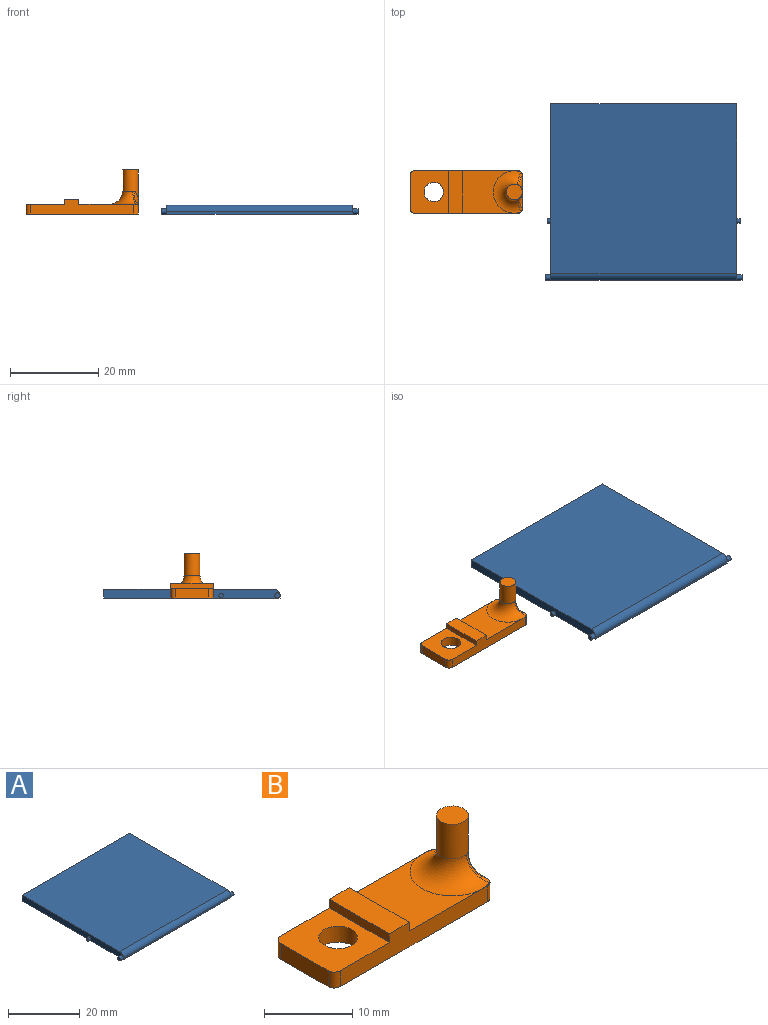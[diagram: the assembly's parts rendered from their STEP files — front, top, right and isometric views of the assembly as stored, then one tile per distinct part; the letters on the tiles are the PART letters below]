
ASSEMBLY  parts=2 mates=1
PART A: 17 faces, bbox 44.6x40x2 mm
  f0: plane 39.98x2mm, normal (1,0,0), area 77.5mm2, adj f3,f6,f7,f12,f14,f16
  f1: plane 39.98x2mm, normal (-1,0,0), area 77.5mm2, adj f3,f6,f7,f8,f10,f16
  f2: plane 0.6x0.56mm, normal (1,0,0), area 0.1mm2, adj f5,f7,f12,f16
  f3: plane 42.2x2mm, normal (0,1,0), area 84.4mm2, adj f0,f1,f6,f7
  f4: plane 0.6x0.56mm, normal (-1,0,0), area 0.1mm2, adj f5,f7,f8,f16
  f5: plane 42.2x0.5mm, normal (0,-1,0), area 21.1mm2, adj f2,f4,f7,f16
  f6: plane 42.2x38.5mm, normal (0,0,1), area 1624.7mm2, adj f0,f1,f3,f16
  f7: plane 42.2x40mm, normal (0,0,-1), area 1688mm2, adj f0,f1,f2,f3,f4,f5
  f8: cylinder r=0.6mm len=1.2mm, axis (1,0,0), area 4.5mm2, adj f1,f4,f9,f16
  f9: plane 1.2x1.2mm, normal (-1,0,0), area 1.1mm2, adj f8
  f10: cylinder r=0.5mm len=1mm, axis (1,0,0), area 2.5mm2, adj f1,f11
  f11: plane 1x1mm, normal (-1,0,0), area 0.8mm2, adj f10
  f12: cylinder r=0.6mm len=1.2mm, axis (-1,0,0), area 4.5mm2, adj f0,f2,f13,f16
  f13: plane 1.2x1.2mm, normal (1,0,0), area 1.1mm2, adj f12
  f14: cylinder r=0.5mm len=1mm, axis (-1,0,0), area 2.5mm2, adj f0,f15
  f15: plane 1x1mm, normal (1,0,0), area 0.8mm2, adj f14
  f16: cylinder r=1.5mm len=42.2mm, axis (-1,0,0), area 99.4mm2, adj f0,f1,f2,f4,f5,f6,f8,f12
PART B: 24 faces, bbox 25.9x15x10 mm
  f0: plane 11.7x9.6mm, normal (0,0,1), area 76.1mm2, adj f5,f9,f17,f22
  f1: plane 1.42x0.21mm, normal (0,0,1), area 0.1mm2, adj f9,f10,f17
  f2: plane 9.6x8.8mm, normal (0,0,1), area 68.8mm2, adj f5,f6,f7,f8,f9,f20,f21
  f3: plane 7.6x2.2mm, normal (1,0,0), area 16.7mm2, adj f4,f10,f12,f15,f19
  f4: cylinder r=1mm len=2.2mm, axis (0,0,-1), area 3.5mm2, adj f3,f5,f11,f12,f18
  f5: plane 23.5x3.4mm, normal (0,1,0), area 55.5mm2, adj f0,f2,f4,f6,f11,f12,f21,f22
  f6: cylinder r=1mm len=2.2mm, axis (0,0,-1), area 3.5mm2, adj f2,f5,f7,f12
  f7: plane 7.6x2.2mm, normal (-1,0,0), area 16.7mm2, adj f2,f6,f8,f12
  f8: cylinder r=1mm len=2.2mm, axis (0,0,-1), area 3.5mm2, adj f2,f7,f9,f12
  f9: plane 23.5x3.4mm, normal (0,-1,0), area 55.5mm2, adj f0,f1,f2,f8,f10,f12,f21,f22
  f10: cylinder r=1mm len=2.2mm, axis (0,0,-1), area 3.5mm2, adj f1,f3,f9,f12,f16
  f11: plane 1.42x0.21mm, normal (0,0,1), area 0.1mm2, adj f4,f5,f17
  f12: plane 25.5x9.6mm, normal (0,0,-1), area 228.7mm2, adj f3,f4,f5,f6,f7,f8,f9,f10
  f13: cylinder r=1.8mm len=7.8mm, axis (0,0,-1), area 59.7mm2, adj f14,f15,f16,f17,f18,f19
  f14: plane 3.6x3.6mm, normal (0,0,1), area 10.2mm2, adj f13
  f15: bspline ~3.92x2.84mm, area 4.9mm2, adj f3,f13,f16
  f16: bspline ~3.34x3.06mm, area 2mm2, adj f10,f13,f15,f17
  f17: torus R=4.8mm, axis (0,0,1), area 51mm2, adj f0,f1,f11,f13,f16,f18
  f18: bspline ~3.33x3.05mm, area 2mm2, adj f4,f13,f17,f19
  f19: bspline ~3.92x2.84mm, area 4.9mm2, adj f3,f13,f18
  f20: cylinder r=2.2mm len=4.4mm, axis (0,0,1), area 30.4mm2, adj f2,f12
  f21: plane 9.6x1.2mm, normal (-1,0,0), area 11.5mm2, adj f2,f5,f9,f23
  f22: plane 9.6x1.2mm, normal (1,0,0), area 11.5mm2, adj f0,f5,f9,f23
  f23: plane 9.6x3.2mm, normal (0,0,1), area 30.7mm2, adj f5,f9,f21,f22
PLACE A t=(40.29,0,0)mm
PLACE B at identity
MATE planar A.f7 <-> B.f12  axis (0,0,-1) through (40.29,0,0)mm
